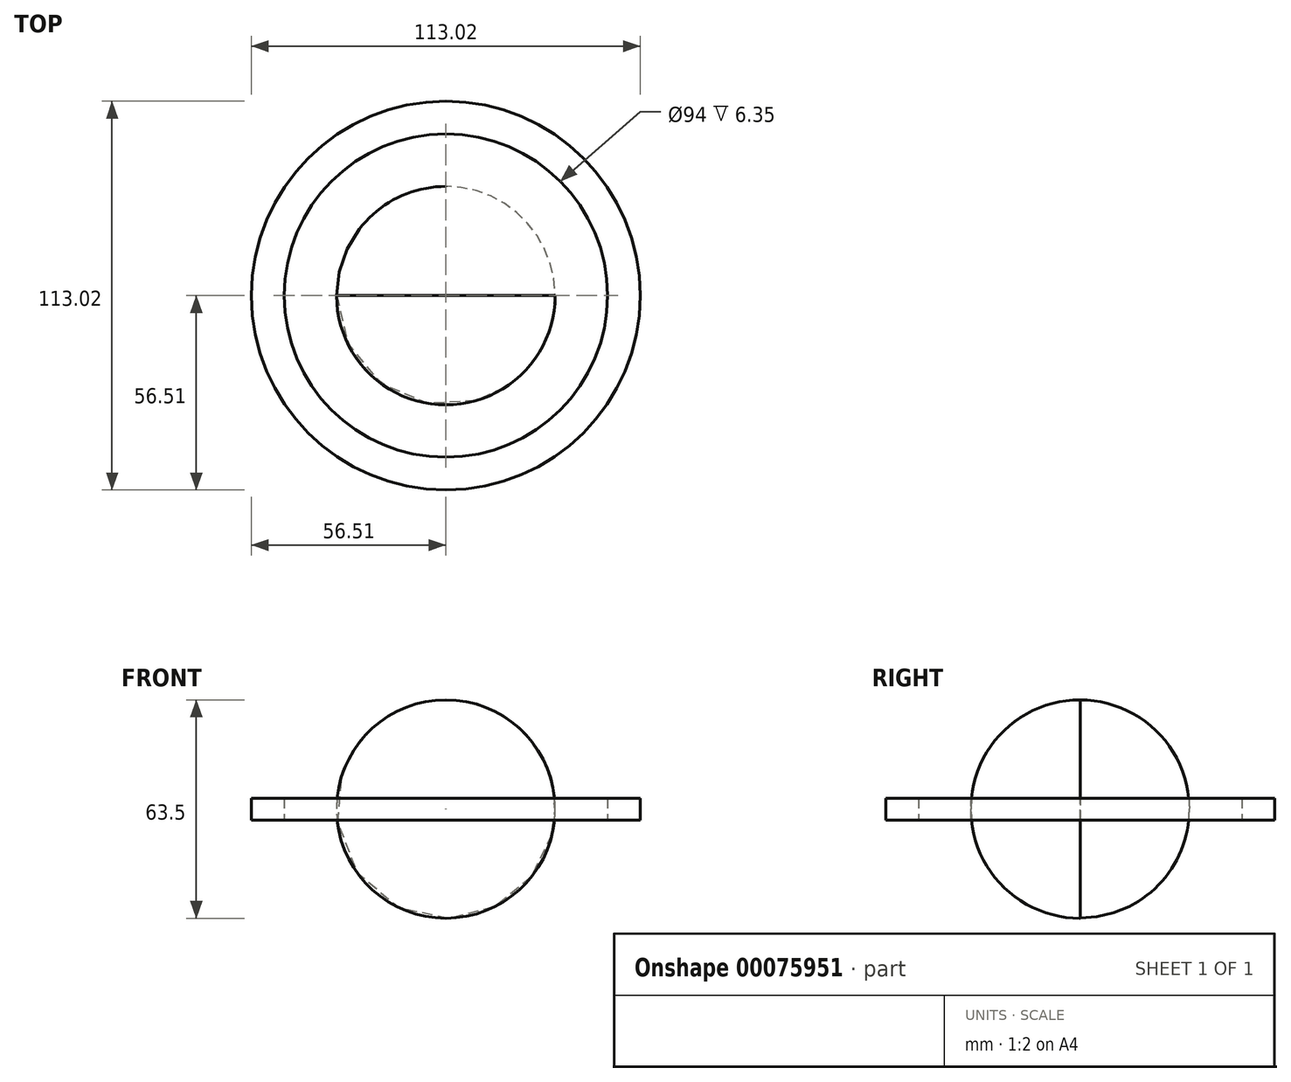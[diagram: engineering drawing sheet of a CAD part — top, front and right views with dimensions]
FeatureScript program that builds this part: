
annotation { "Feature Type Name" : "Feature", "Feature Type Description" : "" }
export const myFeature = defineFeature(function(context is Context, id is Id, definition is map)
    precondition{}
    {
        {
            var Q0;
            Q0=qCreatedBy(makeId("Front.planeOp"),FACE);
            var sketch = newSketch(context, id + "F0", { "sketchPlane" : qUnion([Q0])});
            skCircle(sketch, "E0", {"center": v(0, 0) * mm, "radius": 31.75 * mm});
            skSolve(sketch);
        }
        {
            var Q0;
            Q0=makeQuery(id+"F0.imprint","IMPRINT",FACE,{"disambiguationData":[TD([[makeQuery(id+"F0.imprint","IMPRINT",EDGE,{"derivedFrom":sQuery(id+"F0.wireOp",EDGE,"E0")}),1.0]])]});
            extrude(context, id + "F1", {"entities" : qUnion([Q0]), "endBound" : BoundingType.SYMMETRIC, "depth" : 63.5 * mm});
        }
        {
            var Q0;
            Q0=makeQuery(id+"F1.opExtrude","CAP_EDGE",EDGE,{"disambiguationData":[OSD([sQuery(id+"F0.wireOp",EDGE,"E0")])],"isStart":false});
            fillet(context, id + "F2", {"entities" : qUnion([Q0]), "radius" : 31.71 * mm, "tangentPropagation" : true, "allowEdgeOverflow" : false});
        }
        {
            var Q0;
            Q0=makeQuery(id+"F1.opExtrude","CAP_EDGE",EDGE,{"disambiguationData":[OSD([sQuery(id+"F0.wireOp",EDGE,"E0")])],"isStart":true});
            fillet(context, id + "F3", {"entities" : qUnion([Q0]), "radius" : 31.73 * mm, "tangentPropagation" : true, "allowEdgeOverflow" : false});
        }
        {
            var Q0;
            Q0=qCreatedBy(makeId("Top.planeOp"),FACE);
            var sketch = newSketch(context, id + "F4", { "sketchPlane" : qUnion([Q0])});
            skCircle(sketch, "E1", {"center": v(0, 0) * mm, "radius": 56.5 * mm});
            skCircle(sketch, "E2", {"center": v(0, 0) * mm, "radius": 47 * mm});
            skSolve(sketch);
        }
        {
            var Q0;
            Q0=makeQuery(id+"F4.imprint","IMPRINT",FACE,{"disambiguationData":[TD([[makeQuery(id+"F4.imprint","IMPRINT",EDGE,{"derivedFrom":sQuery(id+"F4.wireOp",EDGE,"E1")}),1.0]])]});
            extrude(context, id + "F5", {"entities" : qUnion([Q0]), "endBound" : BoundingType.SYMMETRIC, "depth" : 6.35 * mm});
        }
    });
